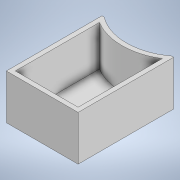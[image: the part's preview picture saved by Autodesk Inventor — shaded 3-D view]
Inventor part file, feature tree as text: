
AUTODESK INVENTOR PART (.ipt)
format: ipt  version: 2022 (Build 260153000, 153)  size: 102,912 bytes
history: native  units: mm
features: extrude x1, shell x1, sketch x1
ambient origin geometry x8: Origin, YZ Plane, XZ Plane, XY Plane, X Axis, Y Axis, Z Axis, Center Point
bodies: Solid1 (feature_tree)
feature tree (3):
  extrude  "Extrusion1"  Depth=160.0mm
  shell  "Shell1"  Thickness=100.0mm
  sketch  "Sketch1"  dims[d0=213.0mm d1=160.0mm d2=100.0mm d3=0.0mm d4=10.0mm d5=250.0mm d6=100.0mm]
